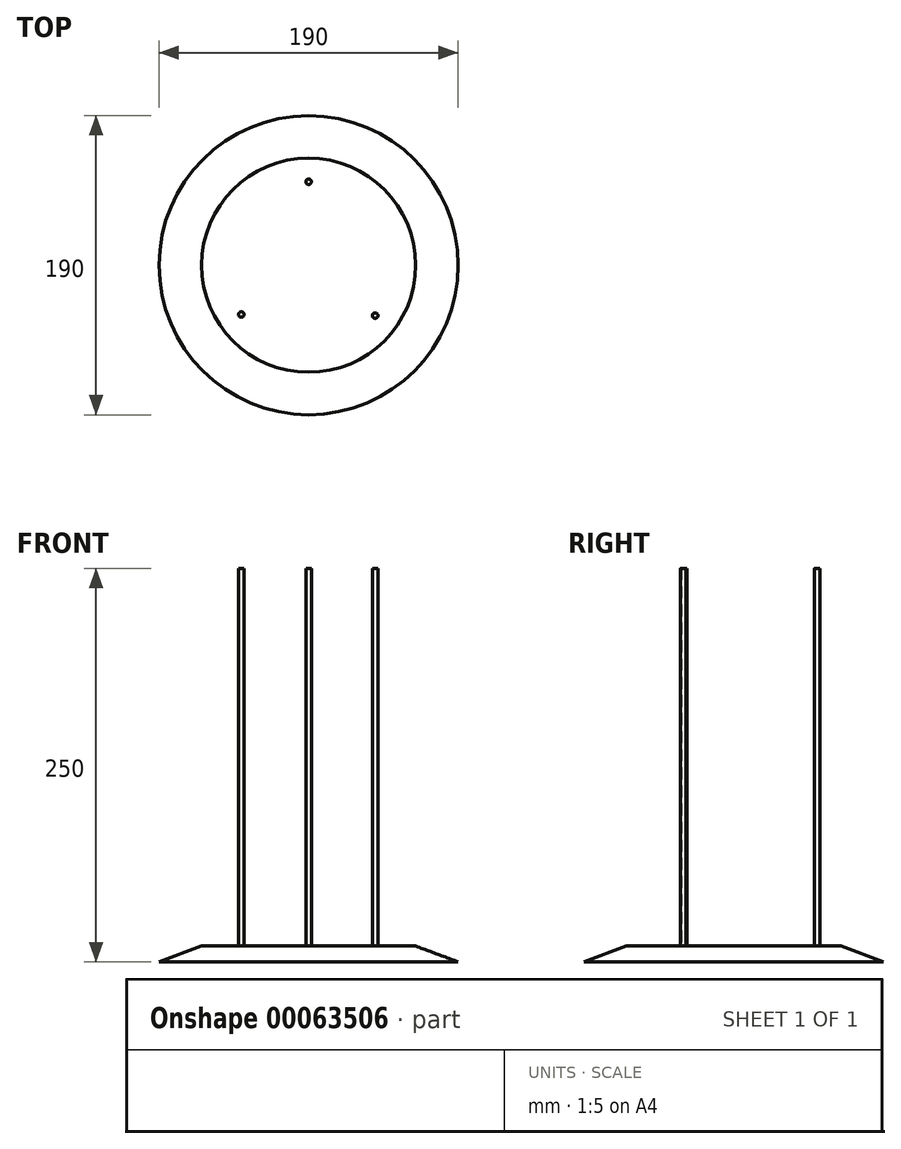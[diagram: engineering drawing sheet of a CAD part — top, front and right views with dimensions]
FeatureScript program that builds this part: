
annotation { "Feature Type Name" : "Feature", "Feature Type Description" : "" }
export const myFeature = defineFeature(function(context is Context, id is Id, definition is map)
    precondition{}
    {
        {
            var Q0;
            Q0=qCreatedBy(makeId("Top.planeOp"),FACE);
            var sketch = newSketch(context, id + "F0", { "sketchPlane" : qUnion([Q0])});
            skCircle(sketch, "E0", {"center": v(0.11, 2.27) * mm, "radius": 50 * mm});
            skCircle(sketch, "E1", {"center": v(0.11, 2.27) * mm, "radius": 45 * mm});
            skCircle(sketch, "E2", {"center": v(-42.64, -29.06) * mm, "radius": 3 * mm});
            skCircle(sketch, "E3", {"center": v(-42.64, -29.06) * mm, "radius": 1.75 * mm});
            skCircle(sketch, "E4", {"center": v(0.11, 55.27) * mm, "radius": 3 * mm});
            skCircle(sketch, "E5", {"center": v(0.11, 55.27) * mm, "radius": 1.75 * mm});
            skCircle(sketch, "E6", {"center": v(42.36, -29.73) * mm, "radius": 3 * mm});
            skCircle(sketch, "E7", {"center": v(42.36, -29.73) * mm, "radius": 1.75 * mm});
            skLineSegment(sketch, "E8", {"start": v(-42.64, -29.06) * mm, "end": v(0.11, 2.27) * mm});
            skLineSegment(sketch, "E9", {"start": v(42.36, -29.73) * mm, "end": v(0.11, 2.27) * mm});
            skLineSegment(sketch, "E10", {"start": v(0.11, 55.27) * mm, "end": v(0.11, 2.27) * mm});
            skArc(sketch, "E11", {"start": v(-43.47, -22.24) * mm, "mid": v(-45.06, -30.83) * mm, "end": v(-36.4, -31.9) * mm});
            skArc(sketch, "E12", {"start": v(36.06, -32.48) * mm, "mid": v(44.75, -31.54) * mm, "end": v(43.3, -22.93) * mm});
            skArc(sketch, "E13", {"start": v(6.1, 51.9) * mm, "mid": v(0.11, 58.27) * mm, "end": v(-5.88, 51.9) * mm});
            skCircle(sketch, "E14", {"center": v(0.11, 2.27) * mm, "radius": 48.5 * mm});
            skCircle(sketch, "E15", {"center": v(0.11, 2.27) * mm, "radius": 46 * mm});
            skCircle(sketch, "E16", {"center": v(0.11, 2.27) * mm, "radius": 67.5 * mm});
            skCircle(sketch, "E17", {"center": v(0.11, 2.27) * mm, "radius": 95 * mm});
            skSolve(sketch);
        }
        {
            var Q0;
            {var subQ0=sQuery(id+"F0.wireOp",EDGE,"E8");var subQ1=sQuery(id+"F0.wireOp",EDGE,"E1");var subQ2=makeQuery(id+"F0.imprint","INTERSECT",VERTEX,{"derivedFrom":[subQ1,subQ0]});Q0=makeQuery(id+"F0.imprint","IMPRINT",FACE,{"disambiguationData":[TD([[makeQuery(id+"F0.imprint","IMPRINT",EDGE,{"disambiguationData":[TD([[subQ2,-1.0]])],"derivedFrom":subQ1}),-1.0]])]});}
            var Q1;
            {var subQ3=sQuery(id+"F0.wireOp",EDGE,"E0");var subQ8=makeQuery(id+"F0.imprint","INTERSECT",VERTEX,{"disambiguationData":[OD(1.0)],"derivedFrom":[subQ3,sQuery(id+"F0.wireOp",EDGE,"E11")]});Q1=makeQuery(id+"F0.imprint","IMPRINT",FACE,{"disambiguationData":[TD([[makeQuery(id+"F0.imprint","IMPRINT",EDGE,{"disambiguationData":[TD([[subQ8,-1.0]])],"derivedFrom":subQ3}),1.0]])]});}
            var Q2;
            {var subQ3=sQuery(id+"F0.wireOp",EDGE,"E0");var subQ5=makeQuery(id+"F0.imprint","INTERSECT",VERTEX,{"disambiguationData":[OD(1.0)],"derivedFrom":[subQ3,sQuery(id+"F0.wireOp",EDGE,"E12")]});Q2=makeQuery(id+"F0.imprint","IMPRINT",FACE,{"disambiguationData":[TD([[makeQuery(id+"F0.imprint","IMPRINT",EDGE,{"disambiguationData":[TD([[subQ5,-1.0]])],"derivedFrom":subQ3}),1.0]])]});}
            var Q3;
            {var subQ0=sQuery(id+"F0.wireOp",EDGE,"E14");var subQ1=sQuery(id+"F0.wireOp",EDGE,"E8");var subQ2=makeQuery(id+"F0.imprint","INTERSECT",VERTEX,{"derivedFrom":[subQ1,subQ0]});Q3=makeQuery(id+"F0.imprint","IMPRINT",FACE,{"disambiguationData":[TD([[makeQuery(id+"F0.imprint","IMPRINT",EDGE,{"disambiguationData":[TD([[subQ2,-1.0]])],"derivedFrom":subQ1}),1.0]])]});}
            var Q4;
            Q4=makeQuery(id+"F0.imprint","IMPRINT",FACE,{"disambiguationData":[TD([[makeQuery(id+"F0.imprint","IMPRINT",EDGE,{"derivedFrom":sQuery(id+"F0.wireOp",EDGE,"E7")}),-1.0]])]});
            var Q5;
            {var subQ0=sQuery(id+"F0.wireOp",EDGE,"E10");var subQ1=sQuery(id+"F0.wireOp",EDGE,"E1");var subQ2=makeQuery(id+"F0.imprint","INTERSECT",VERTEX,{"derivedFrom":[subQ1,subQ0]});Q5=makeQuery(id+"F0.imprint","IMPRINT",FACE,{"disambiguationData":[TD([[makeQuery(id+"F0.imprint","IMPRINT",EDGE,{"disambiguationData":[TD([[subQ2,1.0]])],"derivedFrom":subQ1}),-1.0]])]});}
            var Q6;
            Q6=makeQuery(id+"F0.imprint","IMPRINT",FACE,{"disambiguationData":[TD([[makeQuery(id+"F0.imprint","IMPRINT",EDGE,{"derivedFrom":sQuery(id+"F0.wireOp",EDGE,"E3")}),-1.0]])]});
            var Q7;
            {var subQ0=sQuery(id+"F0.wireOp",EDGE,"E8");var subQ1=sQuery(id+"F0.wireOp",EDGE,"E1");var subQ2=makeQuery(id+"F0.imprint","INTERSECT",VERTEX,{"derivedFrom":[subQ1,subQ0]});Q7=makeQuery(id+"F0.imprint","IMPRINT",FACE,{"disambiguationData":[TD([[makeQuery(id+"F0.imprint","IMPRINT",EDGE,{"disambiguationData":[TD([[subQ2,1.0]])],"derivedFrom":subQ1}),-1.0]])]});}
            var Q8;
            Q8=makeQuery(id+"F0.imprint","IMPRINT",FACE,{"disambiguationData":[TD([[makeQuery(id+"F0.imprint","IMPRINT",EDGE,{"derivedFrom":sQuery(id+"F0.wireOp",EDGE,"E5")}),-1.0]])]});
            var Q9;
            Q9=makeQuery(id+"F0.imprint","IMPRINT",FACE,{"disambiguationData":[TD([[makeQuery(id+"F0.imprint","IMPRINT",EDGE,{"derivedFrom":sQuery(id+"F0.wireOp",EDGE,"E3")}),1.0]])]});
            var Q10;
            Q10=makeQuery(id+"F0.imprint","IMPRINT",FACE,{"disambiguationData":[TD([[makeQuery(id+"F0.imprint","IMPRINT",EDGE,{"derivedFrom":sQuery(id+"F0.wireOp",EDGE,"E5")}),1.0]])]});
            var Q11;
            Q11=makeQuery(id+"F0.imprint","IMPRINT",FACE,{"disambiguationData":[TD([[makeQuery(id+"F0.imprint","IMPRINT",EDGE,{"derivedFrom":sQuery(id+"F0.wireOp",EDGE,"E7")}),1.0]])]});
            var Q12;
            Q12=makeQuery(id+"F0.imprint","IMPRINT",FACE,{"disambiguationData":[TD([[makeQuery(id+"F0.imprint","IMPRINT",EDGE,{"derivedFrom":sQuery(id+"F0.wireOp",EDGE,"E16")}),-1.0]])]});
            var Q13;
            {var subQ0=sQuery(id+"F0.wireOp",EDGE,"E13");var subQ1=sQuery(id+"F0.wireOp",EDGE,"E0");var subQ2=makeQuery(id+"F0.imprint","INTERSECT",VERTEX,{"disambiguationData":[OD(0.0)],"derivedFrom":[subQ1,subQ0]});Q13=makeQuery(id+"F0.imprint","IMPRINT",FACE,{"disambiguationData":[TD([[makeQuery(id+"F0.imprint","IMPRINT",EDGE,{"disambiguationData":[TD([[subQ2,-1.0]])],"derivedFrom":subQ0}),1.0]])]});}
            var Q14;
            {var subQ0=sQuery(id+"F0.wireOp",EDGE,"E13");var subQ1=sQuery(id+"F0.wireOp",EDGE,"E0");var subQ2=makeQuery(id+"F0.imprint","INTERSECT",VERTEX,{"disambiguationData":[OD(1.0)],"derivedFrom":[subQ1,subQ0]});Q14=makeQuery(id+"F0.imprint","IMPRINT",FACE,{"disambiguationData":[TD([[makeQuery(id+"F0.imprint","IMPRINT",EDGE,{"disambiguationData":[TD([[subQ2,1.0]])],"derivedFrom":subQ0}),1.0]])]});}
            var Q15;
            {var subQ0=sQuery(id+"F0.wireOp",EDGE,"E11");var subQ1=sQuery(id+"F0.wireOp",EDGE,"E0");var subQ2=makeQuery(id+"F0.imprint","INTERSECT",VERTEX,{"disambiguationData":[OD(0.0)],"derivedFrom":[subQ1,subQ0]});Q15=makeQuery(id+"F0.imprint","IMPRINT",FACE,{"disambiguationData":[TD([[makeQuery(id+"F0.imprint","IMPRINT",EDGE,{"disambiguationData":[TD([[subQ2,-1.0]])],"derivedFrom":subQ0}),1.0]])]});}
            var Q16;
            {var subQ0=sQuery(id+"F0.wireOp",EDGE,"E11");var subQ1=sQuery(id+"F0.wireOp",EDGE,"E0");var subQ2=makeQuery(id+"F0.imprint","INTERSECT",VERTEX,{"disambiguationData":[OD(1.0)],"derivedFrom":[subQ1,subQ0]});Q16=makeQuery(id+"F0.imprint","IMPRINT",FACE,{"disambiguationData":[TD([[makeQuery(id+"F0.imprint","IMPRINT",EDGE,{"disambiguationData":[TD([[subQ2,1.0]])],"derivedFrom":subQ0}),1.0]])]});}
            var Q17;
            {var subQ0=sQuery(id+"F0.wireOp",EDGE,"E12");var subQ1=sQuery(id+"F0.wireOp",EDGE,"E0");var subQ2=makeQuery(id+"F0.imprint","INTERSECT",VERTEX,{"disambiguationData":[OD(0.0)],"derivedFrom":[subQ1,subQ0]});Q17=makeQuery(id+"F0.imprint","IMPRINT",FACE,{"disambiguationData":[TD([[makeQuery(id+"F0.imprint","IMPRINT",EDGE,{"disambiguationData":[TD([[subQ2,-1.0]])],"derivedFrom":subQ0}),1.0]])]});}
            var Q18;
            {var subQ0=sQuery(id+"F0.wireOp",EDGE,"E12");var subQ1=sQuery(id+"F0.wireOp",EDGE,"E0");var subQ2=makeQuery(id+"F0.imprint","INTERSECT",VERTEX,{"disambiguationData":[OD(1.0)],"derivedFrom":[subQ1,subQ0]});Q18=makeQuery(id+"F0.imprint","IMPRINT",FACE,{"disambiguationData":[TD([[makeQuery(id+"F0.imprint","IMPRINT",EDGE,{"disambiguationData":[TD([[subQ2,1.0]])],"derivedFrom":subQ0}),1.0]])]});}
            var Q19;
            {var subQ0=sQuery(id+"F0.wireOp",EDGE,"E8");var subQ1=sQuery(id+"F0.wireOp",EDGE,"E1");var subQ2=makeQuery(id+"F0.imprint","INTERSECT",VERTEX,{"derivedFrom":[subQ1,subQ0]});Q19=makeQuery(id+"F0.imprint","IMPRINT",FACE,{"disambiguationData":[TD([[makeQuery(id+"F0.imprint","IMPRINT",EDGE,{"disambiguationData":[TD([[subQ2,1.0]])],"derivedFrom":subQ1}),1.0]])]});}
            var Q20;
            {var subQ0=sQuery(id+"F0.wireOp",EDGE,"E8");var subQ1=sQuery(id+"F0.wireOp",EDGE,"E1");var subQ2=makeQuery(id+"F0.imprint","INTERSECT",VERTEX,{"derivedFrom":[subQ1,subQ0]});Q20=makeQuery(id+"F0.imprint","IMPRINT",FACE,{"disambiguationData":[TD([[makeQuery(id+"F0.imprint","IMPRINT",EDGE,{"disambiguationData":[TD([[subQ2,-1.0]])],"derivedFrom":subQ1}),1.0]])]});}
            var Q21;
            {var subQ0=sQuery(id+"F0.wireOp",EDGE,"E10");var subQ1=sQuery(id+"F0.wireOp",EDGE,"E1");var subQ2=makeQuery(id+"F0.imprint","INTERSECT",VERTEX,{"derivedFrom":[subQ1,subQ0]});Q21=makeQuery(id+"F0.imprint","IMPRINT",FACE,{"disambiguationData":[TD([[makeQuery(id+"F0.imprint","IMPRINT",EDGE,{"disambiguationData":[TD([[subQ2,1.0]])],"derivedFrom":subQ1}),1.0]])]});}
            var Q22;
            Q22=makeQuery(id+"F0.imprint","IMPRINT",FACE,{"disambiguationData":[TD([[makeQuery(id+"F0.imprint","IMPRINT",EDGE,{"derivedFrom":sQuery(id+"F0.wireOp",EDGE,"E16")}),1.0]])]});
            var Q23;
            {var subQ0=sQuery(id+"F0.wireOp",EDGE,"E14");var subQ1=sQuery(id+"F0.wireOp",EDGE,"E8");var subQ2=makeQuery(id+"F0.imprint","INTERSECT",VERTEX,{"derivedFrom":[subQ1,subQ0]});Q23=makeQuery(id+"F0.imprint","IMPRINT",FACE,{"disambiguationData":[TD([[makeQuery(id+"F0.imprint","IMPRINT",EDGE,{"disambiguationData":[TD([[subQ2,-1.0]])],"derivedFrom":subQ1}),-1.0]])]});}
            var Q24;
            {var subQ0=sQuery(id+"F0.wireOp",EDGE,"E14");var subQ1=sQuery(id+"F0.wireOp",EDGE,"E9");var subQ2=makeQuery(id+"F0.imprint","INTERSECT",VERTEX,{"derivedFrom":[subQ1,subQ0]});Q24=makeQuery(id+"F0.imprint","IMPRINT",FACE,{"disambiguationData":[TD([[makeQuery(id+"F0.imprint","IMPRINT",EDGE,{"disambiguationData":[TD([[subQ2,-1.0]])],"derivedFrom":subQ1}),-1.0]])]});}
            var Q25;
            {var subQ3=sQuery(id+"F0.wireOp",EDGE,"E0");var subQ8=makeQuery(id+"F0.imprint","INTERSECT",VERTEX,{"disambiguationData":[OD(0.0)],"derivedFrom":[subQ3,sQuery(id+"F0.wireOp",EDGE,"E11")]});Q25=makeQuery(id+"F0.imprint","IMPRINT",FACE,{"disambiguationData":[TD([[makeQuery(id+"F0.imprint","IMPRINT",EDGE,{"disambiguationData":[TD([[subQ8,1.0]])],"derivedFrom":subQ3}),1.0]])]});}
            extrude(context, id + "F1", {"entities" : qUnion([Q0, Q1, Q2, Q3, Q4, Q5, Q6, Q7, Q8, Q9, Q10, Q11, Q12, Q13, Q14, Q15, Q16, Q17, Q18, Q19, Q20, Q21, Q22, Q23, Q24, Q25]), "depth" : 10 * mm});
        }
        {
            var Q0;
            Q0=makeQuery(id+"F0.imprint","IMPRINT",FACE,{"disambiguationData":[TD([[makeQuery(id+"F0.imprint","IMPRINT",EDGE,{"derivedFrom":sQuery(id+"F0.wireOp",EDGE,"E3")}),1.0]])]});
            var Q1;
            Q1=makeQuery(id+"F0.imprint","IMPRINT",FACE,{"disambiguationData":[TD([[makeQuery(id+"F0.imprint","IMPRINT",EDGE,{"derivedFrom":sQuery(id+"F0.wireOp",EDGE,"E7")}),1.0]])]});
            var Q2;
            Q2=makeQuery(id+"F0.imprint","IMPRINT",FACE,{"disambiguationData":[TD([[makeQuery(id+"F0.imprint","IMPRINT",EDGE,{"derivedFrom":sQuery(id+"F0.wireOp",EDGE,"E5")}),1.0]])]});
            extrude(context, id + "F2", {"entities" : qUnion([Q0, Q1, Q2]), "operationType" : NewBodyOperationType.ADD, "depth" : 250 * mm});
        }
        {
            var Q0;
            Q0=makeQuery(id+"F1.opExtrude","CAP_EDGE",EDGE,{"disambiguationData":[OSD([sQuery(id+"F0.wireOp",EDGE,"E17")])],"isStart":false});
            chamfer(context, id + "F3", {"entities" : qUnion([Q0]), "chamferType" : ChamferType.TWO_OFFSETS, "width1" : 27 * mm, "oppositeDirection" : false, "width2" : 10 * mm, "tangentPropagation" : true});
        }
    });
